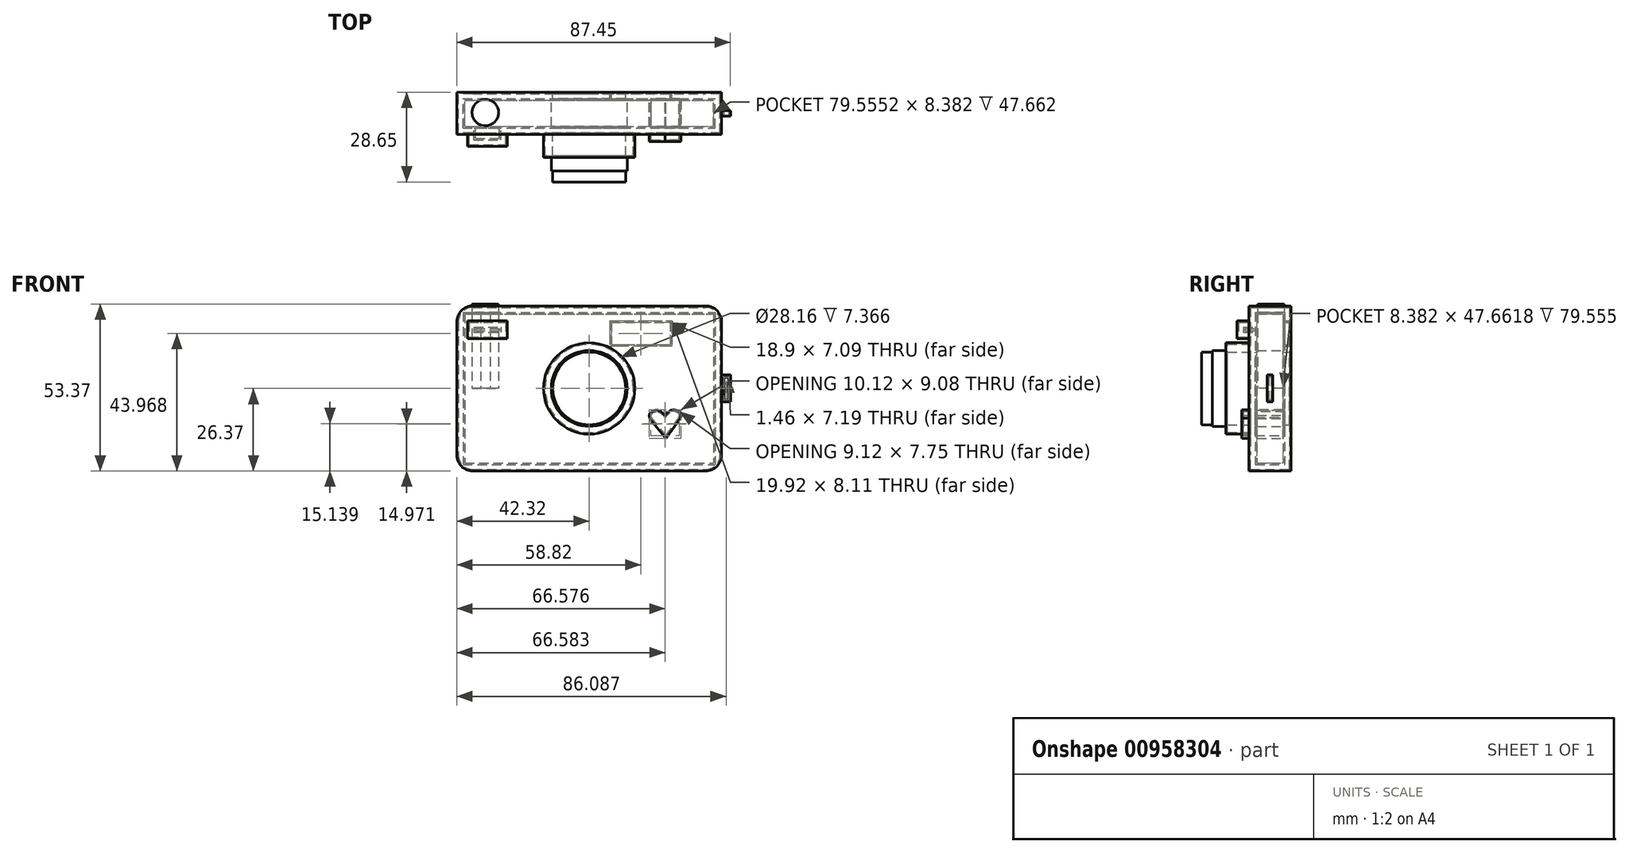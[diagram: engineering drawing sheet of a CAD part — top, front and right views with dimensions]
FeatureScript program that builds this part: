
annotation { "Feature Type Name" : "Feature", "Feature Type Description" : "" }
export const myFeature = defineFeature(function(context is Context, id is Id, definition is map)
    precondition{}
    {
        {
            var Q0;
            Q0=qCreatedBy(makeId("Front.planeOp"),FACE);
            var sketch = newSketch(context, id + "F0", { "sketchPlane" : qUnion([Q0])});
            skLineSegment(sketch, "E0.bottom", {"start": v(-42.32, 26.37) * mm, "end": v(42.32, 26.37) * mm});
            skLineSegment(sketch, "E0.top", {"start": v(-42.32, -26.37) * mm, "end": v(42.32, -26.37) * mm});
            skLineSegment(sketch, "E0.left", {"start": v(-42.32, 26.37) * mm, "end": v(-42.32, -26.37) * mm});
            skLineSegment(sketch, "E0.right", {"start": v(42.32, 26.37) * mm, "end": v(42.32, -26.37) * mm});
            skPoint(sketch, "E0.middle", {"position": v(0, 0) * mm});
            skCircle(sketch, "E1", {"center": v(0, 0) * mm, "radius": 14.59 * mm});
            skLineSegment(sketch, "E2.bottom", {"start": v(-38.87, 21.68) * mm, "end": v(-26.16, 21.68) * mm});
            skLineSegment(sketch, "E2.top", {"start": v(-38.87, 15.88) * mm, "end": v(-26.16, 15.88) * mm});
            skLineSegment(sketch, "E2.left", {"start": v(-38.87, 21.68) * mm, "end": v(-38.87, 15.88) * mm});
            skLineSegment(sketch, "E2.right", {"start": v(-26.16, 21.68) * mm, "end": v(-26.16, 15.88) * mm});
            skPoint(sketch, "E2.middle", {"position": v(-32.51, 18.78) * mm});
            skSolve(sketch);
        }
        {
            var Q0;
            Q0=makeQuery(id+"F0.imprint","IMPRINT",FACE,{"disambiguationData":[TD([[makeQuery(id+"F0.imprint","IMPRINT",EDGE,{"derivedFrom":sQuery(id+"F0.wireOp",EDGE,"E0.bottom")}),-1.0]])]});
            extrude(context, id + "F1", {"entities" : qUnion([Q0]), "depth" : 13.46 * mm, "offsetDistance" : 25.4 * mm});
        }
        {
            var Q0;
            Q0=makeQuery(id+"F0.imprint","IMPRINT",FACE,{"disambiguationData":[TD([[makeQuery(id+"F0.imprint","IMPRINT",EDGE,{"derivedFrom":sQuery(id+"F0.wireOp",EDGE,"E1")}),1.0]])]});
            extrude(context, id + "F2", {"entities" : qUnion([Q0]), "operationType" : NewBodyOperationType.ADD, "depth" : 20.83 * mm, "offsetDistance" : 25.4 * mm});
        }
        {
            var Q0;
            Q0=makeQuery(id+"F0.imprint","IMPRINT",FACE,{"disambiguationData":[TD([[makeQuery(id+"F0.imprint","IMPRINT",EDGE,{"derivedFrom":sQuery(id+"F0.wireOp",EDGE,"E2.bottom")}),-1.0]])]});
            extrude(context, id + "F3", {"entities" : qUnion([Q0]), "operationType" : NewBodyOperationType.ADD, "depth" : 17.27 * mm, "offsetDistance" : 25.4 * mm});
        }
        {
            var Q0;
            Q0=makeQuery(id+"F2.opExtrude","CAP_FACE",FACE,{"disambiguationData":[OSD([sQuery(id+"F0.wireOp",EDGE,"E1")])],"isStart":false});
            shell(context, id + "F4", {"entities" : qUnion([Q0]), "thickness" : 2.54 * mm});
        }
        {
            var Q0;
            {var subQ0=sQuery(id+"F0.wireOp",EDGE,"E2.right");var subQ1=sQuery(id+"F0.wireOp",EDGE,"E2.left");var subQ2=sQuery(id+"F0.wireOp",EDGE,"E2.top");var subQ3=sQuery(id+"F0.wireOp",EDGE,"E2.bottom");var subQ4=sQuery(id+"F0.wireOp",EDGE,"E1");var subQ5=sQuery(id+"F0.wireOp",EDGE,"E0.right");var subQ6=sQuery(id+"F0.wireOp",EDGE,"E0.left");var subQ7=sQuery(id+"F0.wireOp",EDGE,"E0.top");var subQ8=sQuery(id+"F0.wireOp",EDGE,"E0.bottom");Q0=makeQuery(id+"F4.opShell","OFFSET_FACE",FACE,{"disambiguationData":[OSD([subQ8,subQ7,subQ6,subQ5,subQ4,subQ3,subQ2,subQ1,subQ0]),TDD([makeQuery(id+"F3.boolean.opBoolean","MERGE",FACE,{"derivedFrom":[makeQuery(id+"F2.boolean.opBoolean","MERGE",FACE,{"derivedFrom":[makeQuery(id+"F1.opExtrude","CAP_FACE",FACE,{"disambiguationData":[OSD([subQ8,subQ7,subQ6,subQ5,subQ4,subQ3,subQ2,subQ1,subQ0])],"isStart":true}),makeQuery(id+"F2.opExtrude","CAP_FACE",FACE,{"disambiguationData":[OSD([subQ4])],"isStart":true})]}),makeQuery(id+"F3.opExtrude","CAP_FACE",FACE,{"disambiguationData":[OSD([subQ3,subQ2,subQ1,subQ0])],"isStart":true})]})])]});}
            var sketch = newSketch(context, id + "F5", { "sketchPlane" : qUnion([Q0])});
            skCircle(sketch, "E3", {"center": v(0, 0) * mm, "radius": 12.14 * mm});
            skSolve(sketch);
        }
        {
            var Q0;
            Q0 = qSketchRegion(id + "F5", true);
            extrude(context, id + "F6", {"entities" : qUnion([Q0]), "operationType" : NewBodyOperationType.ADD, "depth" : 22.6 * mm, "offsetDistance" : 25.4 * mm});
        }
        {
            var Q0;
            Q0=qCreatedBy(makeId("Top.planeOp"),FACE);
            var sketch = newSketch(context, id + "F7", { "sketchPlane" : qUnion([Q0])});
            skCircle(sketch, "E4", {"center": v(-33.2, -6.49) * mm, "radius": 4.24 * mm});
            skSolve(sketch);
        }
        {
            var Q0;
            Q0=makeQuery(id+"F1.opExtrude","SWEPT_EDGE",EDGE,{"disambiguationData":[OSD([sQuery(id+"F0.wireOp",EDGE,"E0.bottom"),sQuery(id+"F0.wireOp",EDGE,"E0.right")])]});
            cPoint(context, id + "F8", {"entities" : qUnion([Q0]), "parameter" : 0.5});
        }
        {
            var Q0;
            Q0=qCreatedBy(makeId("Front.planeOp"),FACE);
            var Q1;
            Q1 = qCreatedBy(id + "F8" ,VERTEX);
            cPlane(context, id + "F9", {"entities" : qUnion([Q0, Q1]), "cplaneType" : CPlaneType.PLANE_POINT, "offset" : 25.4 * mm, "width" : 152.4 * mm, "height" : 152.4 * mm});
        }
        {
            var Q0;
            Q0=qCreatedBy(id+"F9.planeOp",FACE);
            var sketch = newSketch(context, id + "F10", { "sketchPlane" : qUnion([Q0])});
            skLineSegment(sketch, "E5", {"start": v(45.13, 0) * mm, "end": v(45.13, -4.32) * mm});
            skLineSegment(sketch, "E6", {"start": v(45.13, -4.32) * mm, "end": v(42.26, -4.32) * mm});
            skLineSegment(sketch, "E7.MirrorCS", {"start": v(45.13, 0) * mm, "end": v(45.13, 4.32) * mm});
            skLineSegment(sketch, "E8.MirrorCS", {"start": v(45.13, 4.32) * mm, "end": v(42.26, 4.32) * mm});
            skLineSegment(sketch, "E9", {"start": v(42.26, 4.32) * mm, "end": v(42.26, -4.32) * mm});
            skSolve(sketch);
        }
        {
            var Q0;
            Q0=makeQuery(id+"F10.imprint","IMPRINT",FACE,{"disambiguationData":[TD([[makeQuery(id+"F10.imprint","IMPRINT",EDGE,{"derivedFrom":sQuery(id+"F10.wireOp",EDGE,"E5")}),-1.0]])]});
            extrude(context, id + "F11", {"entities" : qUnion([Q0]), "operationType" : NewBodyOperationType.ADD, "endBound" : BoundingType.SYMMETRIC, "depth" : 1.83 * mm, "offsetDistance" : 25.4 * mm});
        }
        {
            var Q0;
            Q0=makeQuery(id+"F11.opExtrude","CAP_FACE",FACE,{"disambiguationData":[OSD([sQuery(id+"F10.wireOp",EDGE,"E5"),sQuery(id+"F10.wireOp",EDGE,"E6"),sQuery(id+"F10.wireOp",EDGE,"E7.MirrorCS"),sQuery(id+"F10.wireOp",EDGE,"E8.MirrorCS"),sQuery(id+"F10.wireOp",EDGE,"E9")])],"isStart":false});
            var sketch = newSketch(context, id + "F12", { "sketchPlane" : qUnion([Q0])});
            skLineSegment(sketch, "E10.bottom", {"start": v(44.5, 3.6) * mm, "end": v(43.04, 3.6) * mm});
            skLineSegment(sketch, "E10.top", {"start": v(44.5, -3.6) * mm, "end": v(43.04, -3.6) * mm});
            skLineSegment(sketch, "E10.left", {"start": v(44.5, 3.6) * mm, "end": v(44.5, -3.6) * mm});
            skLineSegment(sketch, "E10.right", {"start": v(43.04, 3.6) * mm, "end": v(43.04, -3.6) * mm});
            skPoint(sketch, "E10.middle", {"position": v(43.77, 0) * mm});
            skSolve(sketch);
        }
        {
            var Q0;
            Q0 = qSketchRegion(id + "F12", true);
            extrude(context, id + "F13", {"entities" : qUnion([Q0]), "operationType" : NewBodyOperationType.REMOVE, "endBound" : BoundingType.THROUGH_ALL, "oppositeDirection" : true, "depth" : 25.4 * mm, "offsetDistance" : 25.4 * mm});
        }
        {
            var Q0;
            Q0=makeQuery(id+"F1.opExtrude","SWEPT_EDGE",EDGE,{"disambiguationData":[OSD([sQuery(id+"F0.wireOp",EDGE,"E0.bottom"),sQuery(id+"F0.wireOp",EDGE,"E0.right")])]});
            var Q1;
            Q1=makeQuery(id+"F1.opExtrude","SWEPT_EDGE",EDGE,{"disambiguationData":[OSD([sQuery(id+"F0.wireOp",EDGE,"E0.top"),sQuery(id+"F0.wireOp",EDGE,"E0.right")])]});
            var Q2;
            Q2=makeQuery(id+"F1.opExtrude","SWEPT_EDGE",EDGE,{"disambiguationData":[OSD([sQuery(id+"F0.wireOp",EDGE,"E0.top"),sQuery(id+"F0.wireOp",EDGE,"E0.left")])]});
            var Q3;
            Q3=makeQuery(id+"F1.opExtrude","SWEPT_EDGE",EDGE,{"disambiguationData":[OSD([sQuery(id+"F0.wireOp",EDGE,"E0.bottom"),sQuery(id+"F0.wireOp",EDGE,"E0.left")])]});
            fillet(context, id + "F14", {"entities" : qUnion([Q0, Q1, Q2, Q3]), "radius" : 5.08 * mm, "tangentPropagation" : true, "allowEdgeOverflow" : false});
        }
        {
            var Q0;
            Q0=qCreatedBy(makeId("Front.planeOp"),FACE);
            var sketch = newSketch(context, id + "F15", { "sketchPlane" : qUnion([Q0])});
            skLineSegment(sketch, "E11", {"start": v(19.34, -9.62) * mm, "end": v(24.53, -15.94) * mm});
            skLineSegment(sketch, "E12", {"start": v(24.53, -15.94) * mm, "end": v(29.14, -9.54) * mm});
            skFitSpline(sketch, "E13", {"points": [v(19.34, -9.62) * mm, v(19.34, -8.08) * mm, v(21.61, -6.95) * mm, v(24.28, -8.57) * mm], "startDerivative": vector(-1.51, 5.86) * mm, "endDerivative": vector(6.55, -6.13) * mm});
            skFitSpline(sketch, "E14", {"points": [v(29.14, -9.54) * mm, v(29.14, -7.84) * mm, v(26.63, -6.87) * mm, v(24.28, -8.57) * mm], "startDerivative": vector(1.73, 6.42) * mm, "endDerivative": vector(-5.68, -6.41) * mm});
            skSolve(sketch);
        }
        {
            var Q0;
            Q0 = qSketchRegion(id + "F15", true);
            extrude(context, id + "F16", {"entities" : qUnion([Q0]), "operationType" : NewBodyOperationType.ADD, "depth" : 15.75 * mm, "offsetDistance" : 25.4 * mm});
        }
        {
            var Q0;
            Q0=qCreatedBy(makeId("Front.planeOp"),FACE);
            var sketch = newSketch(context, id + "F17", { "sketchPlane" : qUnion([Q0])});
            skLineSegment(sketch, "E15.bottom", {"start": v(25.95, 14.05) * mm, "end": v(7.05, 14.05) * mm});
            skLineSegment(sketch, "E15.top", {"start": v(25.95, 21.15) * mm, "end": v(7.05, 21.15) * mm});
            skLineSegment(sketch, "E15.left", {"start": v(25.95, 14.05) * mm, "end": v(25.95, 21.15) * mm});
            skLineSegment(sketch, "E15.right", {"start": v(7.05, 14.05) * mm, "end": v(7.05, 21.15) * mm});
            skSolve(sketch);
        }
        {
            var Q0;
            Q0 = qSketchRegion(id + "F17", true);
            extrude(context, id + "F18", {"entities" : qUnion([Q0]), "operationType" : NewBodyOperationType.REMOVE, "depth" : 10 * mm, "offsetDistance" : 25.4 * mm});
        }
        {
            var Q0;
            Q0=makeQuery(id+"F6.opExtrude","CAP_FACE",FACE,{"disambiguationData":[OSD([sQuery(id+"F5.wireOp",EDGE,"E3")])],"isStart":false});
            shell(context, id + "F19", {"entities" : qUnion([Q0]), "thickness" : 0.5 * mm});
        }
        {
            var Q0;
            {var subQ0=sQuery(id+"F0.wireOp",EDGE,"E2.right");var subQ1=sQuery(id+"F0.wireOp",EDGE,"E2.left");var subQ2=sQuery(id+"F0.wireOp",EDGE,"E2.top");var subQ3=sQuery(id+"F0.wireOp",EDGE,"E2.bottom");var subQ4=sQuery(id+"F0.wireOp",EDGE,"E1");var subQ5=sQuery(id+"F0.wireOp",EDGE,"E0.right");var subQ6=sQuery(id+"F0.wireOp",EDGE,"E0.left");var subQ7=sQuery(id+"F0.wireOp",EDGE,"E0.top");var subQ8=sQuery(id+"F0.wireOp",EDGE,"E0.bottom");Q0=makeQuery(id+"F19.opShell","OFFSET_FACE",FACE,{"disambiguationData":[OSD([subQ8,subQ7,subQ6,subQ5,subQ4,subQ3,subQ2,subQ1,subQ0]),TDD([makeQuery(id+"F3.boolean.opBoolean","MERGE",FACE,{"derivedFrom":[makeQuery(id+"F2.boolean.opBoolean","MERGE",FACE,{"derivedFrom":[makeQuery(id+"F1.opExtrude","CAP_FACE",FACE,{"disambiguationData":[OSD([subQ8,subQ7,subQ6,subQ5,subQ4,subQ3,subQ2,subQ1,subQ0])],"isStart":true}),makeQuery(id+"F2.opExtrude","CAP_FACE",FACE,{"disambiguationData":[OSD([subQ4])],"isStart":true})]}),makeQuery(id+"F3.opExtrude","CAP_FACE",FACE,{"disambiguationData":[OSD([subQ3,subQ2,subQ1,subQ0])],"isStart":true})]})])]});}
            var sketch = newSketch(context, id + "F20", { "sketchPlane" : qUnion([Q0])});
            skCircle(sketch, "E16", {"center": v(0, 0) * mm, "radius": 11.65 * mm});
            skSolve(sketch);
        }
        {
            var Q0;
            Q0 = qSketchRegion(id + "F20", true);
            extrude(context, id + "F21", {"entities" : qUnion([Q0]), "operationType" : NewBodyOperationType.ADD, "depth" : 28.14 * mm, "offsetDistance" : 25.4 * mm});
        }
        {
            var Q0;
            Q0 = qSketchRegion(id + "F7", true);
            extrude(context, id + "F22", {"entities" : qUnion([Q0]), "operationType" : NewBodyOperationType.ADD, "depth" : 27 * mm, "offsetDistance" : 25.4 * mm});
        }
    });
